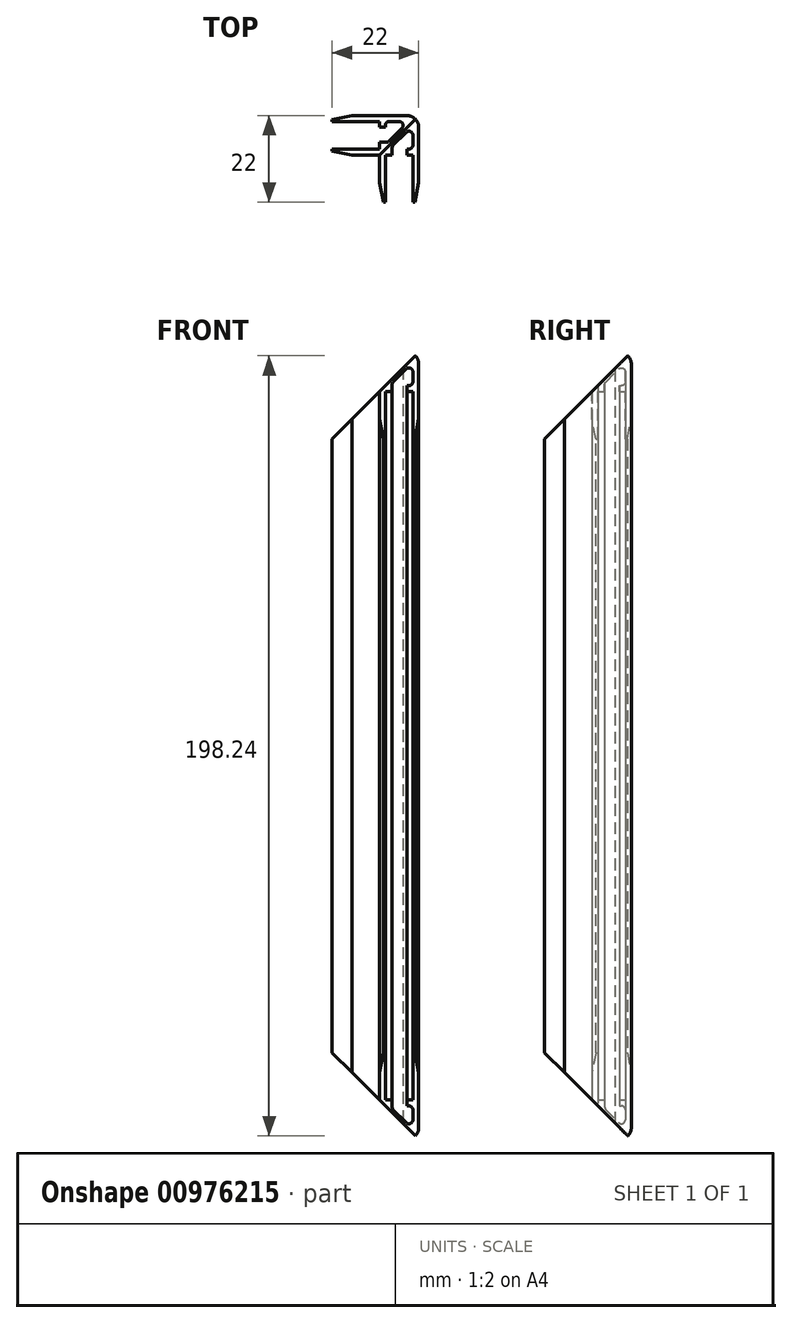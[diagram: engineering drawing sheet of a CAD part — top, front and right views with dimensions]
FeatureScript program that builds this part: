
annotation { "Feature Type Name" : "Feature", "Feature Type Description" : "" }
export const myFeature = defineFeature(function(context is Context, id is Id, definition is map)
    precondition{}
    {
        {
            var Q0;
            Q0=qCreatedBy(makeId("Top.planeOp"),FACE);
            var sketch = newSketch(context, id + "F0", { "sketchPlane" : qUnion([Q0])});
            skLineSegment(sketch, "E0", {"start": v(-22, 0) * mm, "end": v(-3, 0) * mm});
            skLineSegment(sketch, "E1", {"start": v(0, -3) * mm, "end": v(0, -22) * mm});
            skLineSegment(sketch, "E2.0", {"start": v(-10, -10) * mm, "end": v(-10, -22) * mm});
            skLineSegment(sketch, "E2.1", {"start": v(-22, -10) * mm, "end": v(-10, -10) * mm});
            skLineSegment(sketch, "E3.0", {"start": v(-1.5, -2.56) * mm, "end": v(-1.5, -8.5) * mm});
            skLineSegment(sketch, "E3.1", {"start": v(-22, -1.5) * mm, "end": v(-10, -1.5) * mm});
            skLineSegment(sketch, "E4.0", {"start": v(-8.5, -10) * mm, "end": v(-8.5, -22) * mm});
            skLineSegment(sketch, "E4.1", {"start": v(-22, -8.5) * mm, "end": v(-10, -8.5) * mm});
            skLineSegment(sketch, "E5", {"start": v(-22, -8.5) * mm, "end": v(-22, -10) * mm});
            skLineSegment(sketch, "E6", {"start": v(-10, -22) * mm, "end": v(-8.5, -22) * mm});
            skLineSegment(sketch, "E7", {"start": v(-1.5, -22) * mm, "end": v(0, -22) * mm});
            skLineSegment(sketch, "E8", {"start": v(-22, 0) * mm, "end": v(-22, -1.5) * mm});
            skLineSegment(sketch, "E9", {"start": v(-10, -8.5) * mm, "end": v(-10, -6.76) * mm});
            skLineSegment(sketch, "E10", {"start": v(-2.96, -8.5) * mm, "end": v(-1.5, -8.5) * mm});
            skLineSegment(sketch, "E11", {"start": v(-8.5, -10) * mm, "end": v(-6.76, -10) * mm});
            skLineSegment(sketch, "E12.trimOffspring", {"start": v(-8.5, -1.5) * mm, "end": v(-2.56, -1.5) * mm});
            skLineSegment(sketch, "E13.trimOffspring", {"start": v(-1.5, -10) * mm, "end": v(-1.5, -22) * mm});
            skLineSegment(sketch, "E14.0", {"start": v(-6.76, -7.82) * mm, "end": v(-1.5, -2.56) * mm});
            skLineSegment(sketch, "E15.0", {"start": v(-7.82, -6.76) * mm, "end": v(-2.56, -1.5) * mm});
            skLineSegment(sketch, "E16.top", {"start": v(-10, -6.76) * mm, "end": v(-7.82, -6.76) * mm});
            skLineSegment(sketch, "E16.right", {"start": v(-6.76, -10) * mm, "end": v(-6.76, -7.82) * mm});
            skLineSegment(sketch, "E17", {"start": v(-10, -10) * mm, "end": v(0, 0) * mm, "construction": true});
            skLineSegment(sketch, "E18.top", {"start": v(-10, -2.96) * mm, "end": v(-8.5, -2.96) * mm});
            skLineSegment(sketch, "E18.right", {"start": v(-2.96, -10) * mm, "end": v(-2.96, -8.5) * mm});
            skLineSegment(sketch, "E19.trimOffspring", {"start": v(-10, -2.96) * mm, "end": v(-10, -1.5) * mm});
            skLineSegment(sketch, "E20.trimOffspring", {"start": v(-8.5, -2.96) * mm, "end": v(-8.5, -1.5) * mm});
            skLineSegment(sketch, "E21.trimOffspring", {"start": v(-2.96, -10) * mm, "end": v(-1.5, -10) * mm});
            skPoint(sketch, "E22.visualSharp", {"position": v(0, 0) * mm});
            skArc(sketch, "E22.filletArc", {"start": v(0, -3) * mm, "mid": v(-0.88, -0.88) * mm, "end": v(-3, 0) * mm});
            skSolve(sketch);
        }
        {
            var Q0;
            Q0=makeQuery(id+"F0.imprint","IMPRINT",FACE,{"disambiguationData":[TD([[makeQuery(id+"F0.imprint","IMPRINT",EDGE,{"derivedFrom":sQuery(id+"F0.wireOp",EDGE,"E0")}),-1.0]])]});
            extrude(context, id + "F1", {"entities" : qUnion([Q0]), "endBound" : BoundingType.SYMMETRIC, "depth" : 200 * mm, "offsetDistance" : 25 * mm});
        }
        {
            var Q0;
            Q0=makeQuery(id+"F1.opExtrude","SWEPT_EDGE",EDGE,{"disambiguationData":[OSD([sQuery(id+"F0.wireOp",EDGE,"E2.1"),sQuery(id+"F0.wireOp",EDGE,"E5")])]});
            var Q1;
            Q1=makeQuery(id+"F1.opExtrude","SWEPT_EDGE",EDGE,{"disambiguationData":[OSD([sQuery(id+"F0.wireOp",EDGE,"E1"),sQuery(id+"F0.wireOp",EDGE,"E7")])]});
            chamfer(context, id + "F2", {"entities" : qUnion([Q0, Q1]), "chamferType" : ChamferType.TWO_OFFSETS, "width1" : 5 * mm, "oppositeDirection" : false, "width2" : 1 * mm, "tangentPropagation" : true});
        }
        {
            var Q0;
            Q0=makeQuery(id+"F1.opExtrude","SWEPT_EDGE",EDGE,{"disambiguationData":[OSD([sQuery(id+"F0.wireOp",EDGE,"E0"),sQuery(id+"F0.wireOp",EDGE,"E8")])]});
            var Q1;
            Q1=makeQuery(id+"F1.opExtrude","SWEPT_EDGE",EDGE,{"disambiguationData":[OSD([sQuery(id+"F0.wireOp",EDGE,"E2.0"),sQuery(id+"F0.wireOp",EDGE,"E6")])]});
            chamfer(context, id + "F3", {"entities" : qUnion([Q0, Q1]), "chamferType" : ChamferType.TWO_OFFSETS, "width1" : 1 * mm, "oppositeDirection" : false, "width2" : 5 * mm, "tangentPropagation" : true});
        }
        {
            var Q0;
            Q0=makeQuery(id+"F1.opExtrude","SWEPT_EDGE",EDGE,{"disambiguationData":[OSD([sQuery(id+"F0.wireOp",EDGE,"E12.trimOffspring"),sQuery(id+"F0.wireOp",EDGE,"E15.0")])]});
            var Q1;
            Q1=makeQuery(id+"F1.opExtrude","SWEPT_EDGE",EDGE,{"disambiguationData":[OSD([sQuery(id+"F0.wireOp",EDGE,"E3.0"),sQuery(id+"F0.wireOp",EDGE,"E14.0")])]});
            var Q2;
            Q2=makeQuery(id+"F1.opExtrude","SWEPT_EDGE",EDGE,{"disambiguationData":[OSD([sQuery(id+"F0.wireOp",EDGE,"E14.0"),sQuery(id+"F0.wireOp",EDGE,"E16.right")])]});
            var Q3;
            Q3=makeQuery(id+"F1.opExtrude","SWEPT_EDGE",EDGE,{"disambiguationData":[OSD([sQuery(id+"F0.wireOp",EDGE,"E15.0"),sQuery(id+"F0.wireOp",EDGE,"E16.top")])]});
            var Q4;
            Q4=makeQuery(id+"F1.opExtrude","SWEPT_EDGE",EDGE,{"disambiguationData":[OSD([sQuery(id+"F0.wireOp",EDGE,"E3.0"),sQuery(id+"F0.wireOp",EDGE,"E10")])]});
            var Q5;
            Q5=makeQuery(id+"F1.opExtrude","SWEPT_EDGE",EDGE,{"disambiguationData":[OSD([sQuery(id+"F0.wireOp",EDGE,"E12.trimOffspring"),sQuery(id+"F0.wireOp",EDGE,"E20.trimOffspring")])]});
            fillet(context, id + "F4", {"entities" : qUnion([Q0, Q1, Q2, Q3, Q4, Q5]), "radius" : 1 * mm, "tangentPropagation" : true, "allowEdgeOverflow" : false});
        }
        {
            var Q0;
            Q0=qCreatedBy(makeId("Front.planeOp"),FACE);
            var sketch = newSketch(context, id + "F5", { "sketchPlane" : qUnion([Q0])});
            skLineSegment(sketch, "E23", {"start": v(-22, 100) * mm, "end": v(-22, 78) * mm});
            skLineSegment(sketch, "E24", {"start": v(-22, 78) * mm, "end": v(0, 100) * mm});
            skLineSegment(sketch, "E25", {"start": v(0, 100) * mm, "end": v(-22, 100) * mm});
            skLineSegment(sketch, "E26", {"start": v(-22.02, 0) * mm, "end": v(0, 0) * mm, "construction": true});
            skLineSegment(sketch, "E27.MirrorCS", {"start": v(-22, -100) * mm, "end": v(-22, -78) * mm});
            skLineSegment(sketch, "E28.MirrorCS", {"start": v(0, -100) * mm, "end": v(-22, -100) * mm});
            skLineSegment(sketch, "E29.MirrorCS", {"start": v(-22, -78) * mm, "end": v(0, -100) * mm});
            skSolve(sketch);
        }
        {
            var Q0;
            Q0=qCreatedBy(makeId("Right.planeOp"),FACE);
            var sketch = newSketch(context, id + "F6", { "sketchPlane" : qUnion([Q0])});
            skLineSegment(sketch, "E30", {"start": v(0, 100) * mm, "end": v(-22, 100) * mm});
            skLineSegment(sketch, "E31", {"start": v(-22, 100) * mm, "end": v(-22, 78) * mm});
            skLineSegment(sketch, "E32", {"start": v(-22, 78) * mm, "end": v(0, 100) * mm});
            skLineSegment(sketch, "E33", {"start": v(0, 0) * mm, "end": v(-34.5, 0) * mm, "construction": true});
            skLineSegment(sketch, "E34.MirrorCS", {"start": v(0, -100) * mm, "end": v(-22, -100) * mm});
            skLineSegment(sketch, "E35.MirrorCS", {"start": v(-22, -78) * mm, "end": v(0, -100) * mm});
            skLineSegment(sketch, "E36.MirrorCS", {"start": v(-22, -100) * mm, "end": v(-22, -78) * mm});
            skSolve(sketch);
        }
        {
            var Q0;
            Q0=qSketchRegion(id+"F5",true);
            extrude(context, id + "F7", {"entities" : qUnion([Q0]), "operationType" : NewBodyOperationType.REMOVE, "depth" : 25 * mm, "offsetDistance" : 25 * mm});
        }
        {
            var Q0;
            Q0=qSketchRegion(id+"F6",true);
            extrude(context, id + "F8", {"entities" : qUnion([Q0]), "operationType" : NewBodyOperationType.REMOVE, "oppositeDirection" : true, "depth" : 25 * mm, "offsetDistance" : 25 * mm});
        }
    });
